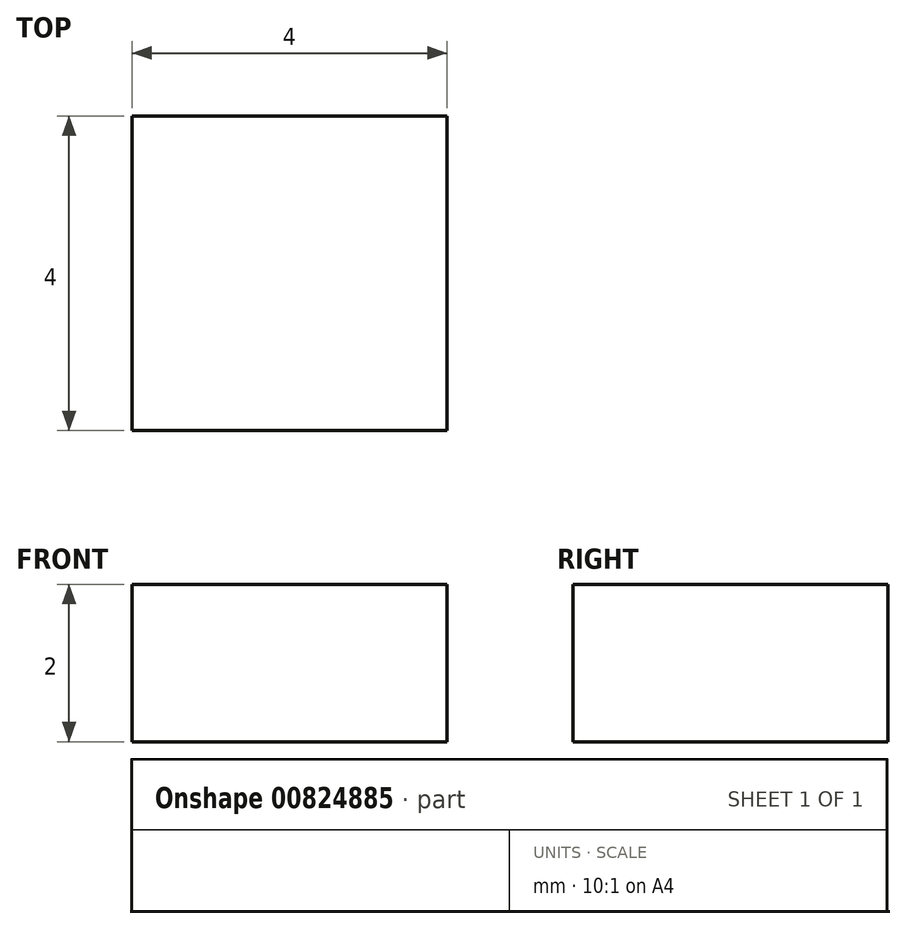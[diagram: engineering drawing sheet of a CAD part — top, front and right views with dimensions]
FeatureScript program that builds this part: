
annotation { "Feature Type Name" : "Feature", "Feature Type Description" : "" }
export const myFeature = defineFeature(function(context is Context, id is Id, definition is map)
    precondition{}
    {
        {
            var Q0;
            Q0=qCreatedBy(makeId("Top.planeOp"),FACE);
            var sketch = newSketch(context, id + "F0", { "sketchPlane" : qUnion([Q0])});
            skLineSegment(sketch, "E0.bottom", {"start": v(2, -2) * mm, "end": v(-2, -2) * mm});
            skLineSegment(sketch, "E0.top", {"start": v(2, 2) * mm, "end": v(-2, 2) * mm});
            skLineSegment(sketch, "E0.left", {"start": v(2, -2) * mm, "end": v(2, 2) * mm});
            skLineSegment(sketch, "E0.right", {"start": v(-2, -2) * mm, "end": v(-2, 2) * mm});
            skPoint(sketch, "E0.middle", {"position": v(0, 0) * mm});
            skSolve(sketch);
        }
        {
            var Q0;
            Q0 = qSketchRegion(id + "F0", true);
            extrude(context, id + "F1", {"entities" : qUnion([Q0]), "depth" : 2 * mm, "offsetDistance" : 25 * mm});
        }
    });
